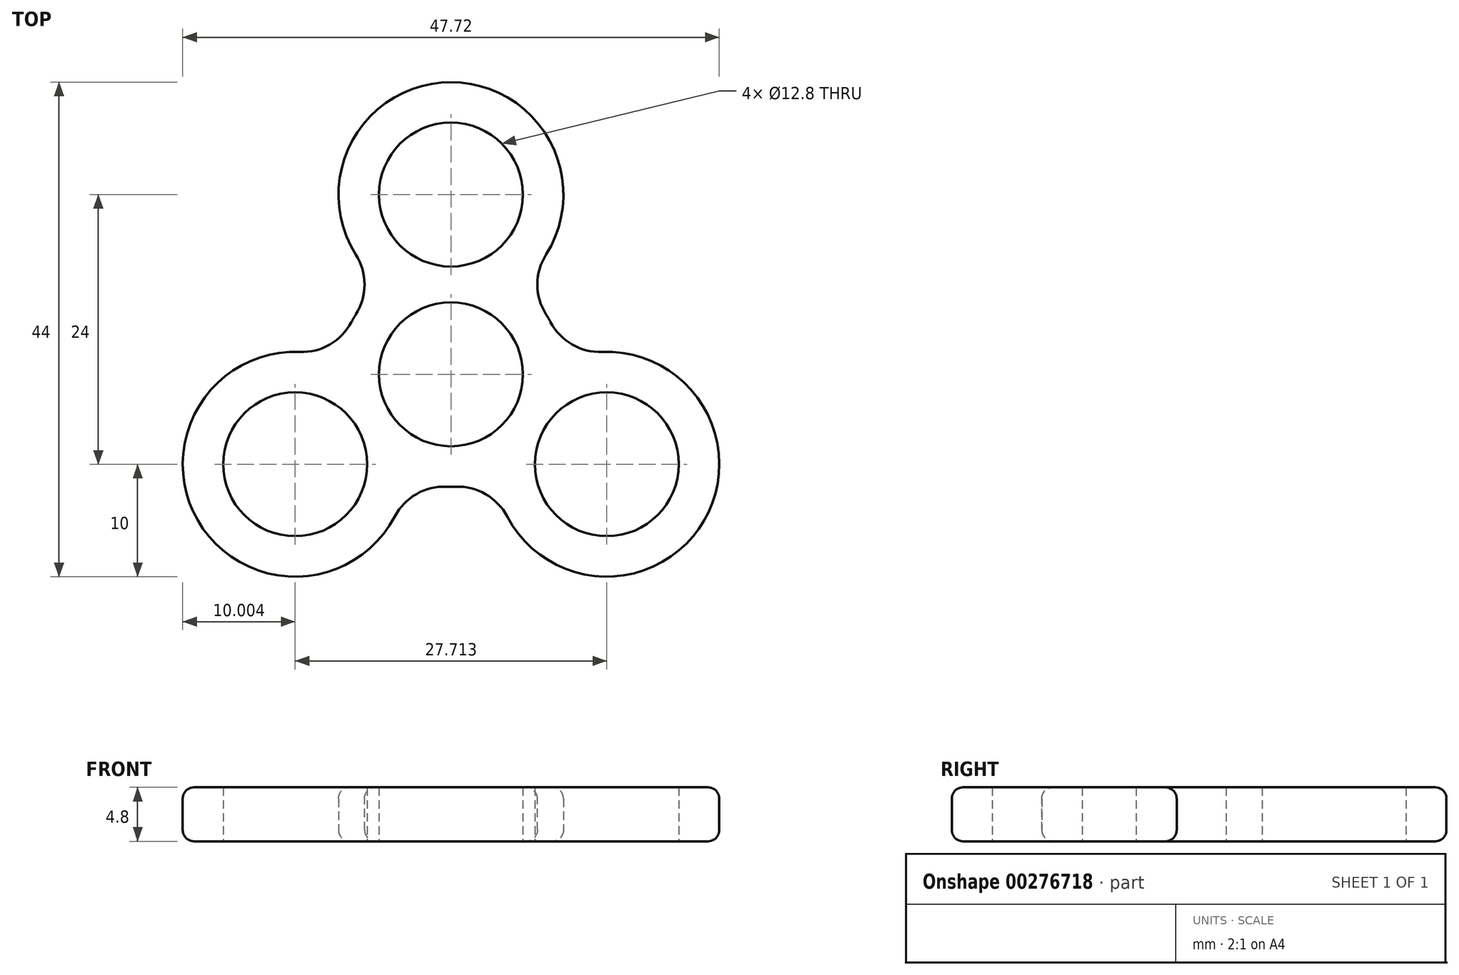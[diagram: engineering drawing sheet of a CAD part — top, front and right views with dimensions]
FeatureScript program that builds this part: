
annotation { "Feature Type Name" : "Feature", "Feature Type Description" : "" }
export const myFeature = defineFeature(function(context is Context, id is Id, definition is map)
    precondition{}
    {
        {
            var Q0;
            Q0=qCreatedBy(makeId("Top.planeOp"),FACE);
            var sketch = newSketch(context, id + "F0", { "sketchPlane" : qUnion([Q0])});
            skCircle(sketch, "E0", {"center": v(0, 0) * mm, "radius": 6.4 * mm});
            skCircle(sketch, "E1", {"center": v(0, 16) * mm, "radius": 6.4 * mm});
            skArc(sketch, "E2", {"start": v(6, 8) * mm, "mid": v(0, 26) * mm, "end": v(-6, 8) * mm});
            skArc(sketch, "E3", {"start": v(-3.93, -9.2) * mm, "mid": v(0, -10) * mm, "end": v(3.93, -9.2) * mm});
            skCircle(sketch, "E4.1.0", {"center": v(-13.86, -8) * mm, "radius": 6.4 * mm});
            skArc(sketch, "E4.1.1", {"start": v(-9.93, 1.2) * mm, "mid": v(-22.52, -13) * mm, "end": v(-3.93, -9.2) * mm});
            skCircle(sketch, "E4.2.0", {"center": v(13.86, -8) * mm, "radius": 6.4 * mm});
            skArc(sketch, "E5.trimOffspring", {"start": v(-6, 8) * mm, "mid": v(-8.66, 5) * mm, "end": v(-9.93, 1.2) * mm});
            skArc(sketch, "E6.trimOffspring", {"start": v(9.93, 1.2) * mm, "mid": v(8.66, 5) * mm, "end": v(6, 8) * mm});
            skArc(sketch, "E7.trimOffspring", {"start": v(3.93, -9.2) * mm, "mid": v(22.52, -13) * mm, "end": v(9.93, 1.2) * mm});
            skSolve(sketch);
        }
        {
            var Q0;
            Q0 = qSketchRegion(id + "F0", true);
            extrude(context, id + "F1", {"entities" : qUnion([Q0]), "depth" : 4.8 * mm});
        }
        {
            var Q0;
            Q0=makeQuery(id+"F1.opExtrude","SWEPT_EDGE",EDGE,{"disambiguationData":[OSD([sQuery(id+"F0.wireOp",EDGE,"E2"),sQuery(id+"F0.wireOp",EDGE,"E6.trimOffspring")])]});
            var Q1;
            Q1=makeQuery(id+"F1.opExtrude","SWEPT_EDGE",EDGE,{"disambiguationData":[OSD([sQuery(id+"F0.wireOp",EDGE,"E6.trimOffspring"),sQuery(id+"F0.wireOp",EDGE,"E7.trimOffspring")])]});
            var Q2;
            Q2=makeQuery(id+"F1.opExtrude","SWEPT_EDGE",EDGE,{"disambiguationData":[OSD([sQuery(id+"F0.wireOp",EDGE,"E3"),sQuery(id+"F0.wireOp",EDGE,"E7.trimOffspring")])]});
            var Q3;
            Q3=makeQuery(id+"F1.opExtrude","SWEPT_EDGE",EDGE,{"disambiguationData":[OSD([sQuery(id+"F0.wireOp",EDGE,"E3"),sQuery(id+"F0.wireOp",EDGE,"E4.1.1")])]});
            var Q4;
            Q4=makeQuery(id+"F1.opExtrude","SWEPT_EDGE",EDGE,{"disambiguationData":[OSD([sQuery(id+"F0.wireOp",EDGE,"E4.1.1"),sQuery(id+"F0.wireOp",EDGE,"E5.trimOffspring")])]});
            var Q5;
            Q5=makeQuery(id+"F1.opExtrude","SWEPT_EDGE",EDGE,{"disambiguationData":[OSD([sQuery(id+"F0.wireOp",EDGE,"E2"),sQuery(id+"F0.wireOp",EDGE,"E5.trimOffspring")])]});
            fillet(context, id + "F2", {"entities" : qUnion([Q0, Q1, Q2, Q3, Q4, Q5]), "radius" : 5 * mm, "tangentPropagation" : true, "allowEdgeOverflow" : false});
        }
        {
            var Q0;
            {var subQ0=sQuery(id+"F0.wireOp",EDGE,"E5.trimOffspring");var subQ1=sQuery(id+"F0.wireOp",EDGE,"E2");Q0=makeQuery(id+"F2.opFillet","BLEND_EDGE",EDGE,{"blendedFrom":[makeQuery(id+"F1.opExtrude","SWEPT_EDGE",EDGE,{"disambiguationData":[OSD([subQ1,subQ0])]}),makeQuery(id+"F1.opExtrude","CAP_FACE",FACE,{"disambiguationData":[OSD([sQuery(id+"F0.wireOp",EDGE,"E0"),sQuery(id+"F0.wireOp",EDGE,"E1"),subQ1,sQuery(id+"F0.wireOp",EDGE,"E3"),sQuery(id+"F0.wireOp",EDGE,"E4.1.0"),sQuery(id+"F0.wireOp",EDGE,"E4.1.1"),sQuery(id+"F0.wireOp",EDGE,"E4.2.0"),subQ0,sQuery(id+"F0.wireOp",EDGE,"E6.trimOffspring"),sQuery(id+"F0.wireOp",EDGE,"E7.trimOffspring")])],"isStart":true})],"blendedInto":[makeQuery(id+"F1.opExtrude","CAP_FACE",FACE,{"disambiguationData":[OSD([sQuery(id+"F0.wireOp",EDGE,"E0"),sQuery(id+"F0.wireOp",EDGE,"E1"),subQ1,sQuery(id+"F0.wireOp",EDGE,"E3"),sQuery(id+"F0.wireOp",EDGE,"E4.1.0"),sQuery(id+"F0.wireOp",EDGE,"E4.1.1"),sQuery(id+"F0.wireOp",EDGE,"E4.2.0"),subQ0,sQuery(id+"F0.wireOp",EDGE,"E6.trimOffspring"),sQuery(id+"F0.wireOp",EDGE,"E7.trimOffspring")])],"isStart":true})]});}
            var Q1;
            Q1=makeQuery(id+"F1.opExtrude","CAP_EDGE",EDGE,{"disambiguationData":[OSD([sQuery(id+"F0.wireOp",EDGE,"E2")])],"isStart":false});
            fillet(context, id + "F3", {"entities" : qUnion([Q0, Q1]), "radius" : 1 * mm, "tangentPropagation" : true, "allowEdgeOverflow" : false});
        }
    });
